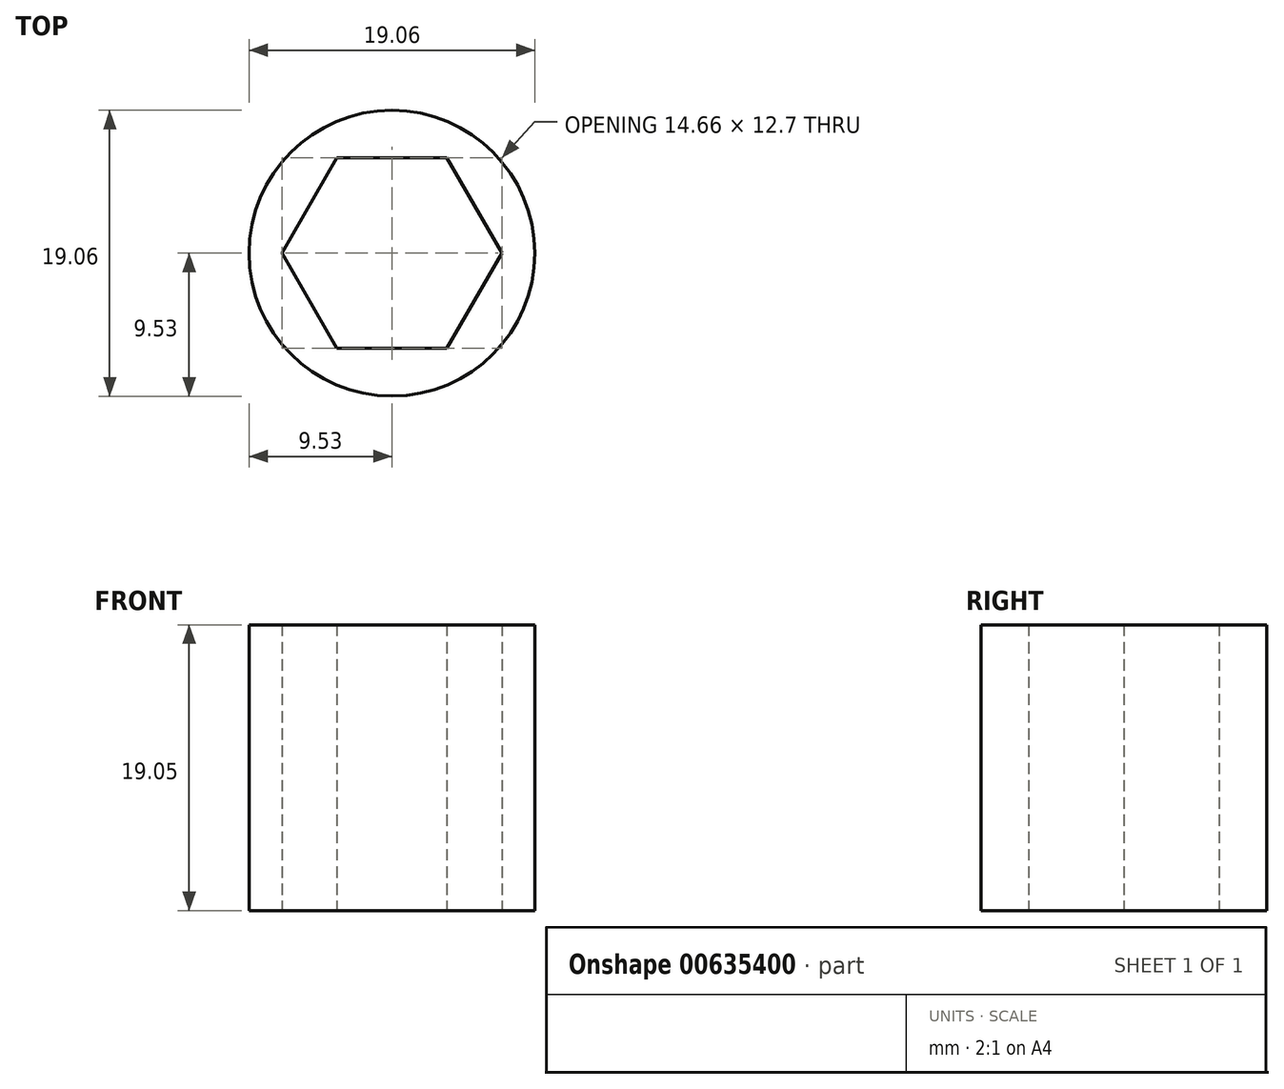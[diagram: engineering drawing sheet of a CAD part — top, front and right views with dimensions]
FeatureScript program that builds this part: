
annotation { "Feature Type Name" : "Feature", "Feature Type Description" : "" }
export const myFeature = defineFeature(function(context is Context, id is Id, definition is map)
    precondition{}
    {
        {
            var Q0;
            Q0=qCreatedBy(makeId("Top.planeOp"),FACE);
            var sketch = newSketch(context, id + "F0", { "sketchPlane" : qUnion([Q0])});
            skCircle(sketch, "E0.cCircle", {"center": v(0, 0) * mm, "radius": 6.35 * mm, "construction": true});
            skLineSegment(sketch, "E0.0", {"start": v(-3.67, 6.35) * mm, "end": v(3.67, 6.35) * mm});
            skLineSegment(sketch, "E0.1", {"start": v(3.67, 6.35) * mm, "end": v(7.33, 0) * mm});
            skLineSegment(sketch, "E0.2", {"start": v(7.33, 0) * mm, "end": v(3.67, -6.35) * mm});
            skLineSegment(sketch, "E0.3", {"start": v(3.67, -6.35) * mm, "end": v(-3.67, -6.35) * mm});
            skLineSegment(sketch, "E0.4", {"start": v(-3.67, -6.35) * mm, "end": v(-7.33, 0) * mm});
            skLineSegment(sketch, "E0.5", {"start": v(-7.33, 0) * mm, "end": v(-3.67, 6.35) * mm});
            skPoint(sketch, "E0.0.midPoint", {"position": v(0, 6.35) * mm});
            skCircle(sketch, "E1", {"center": v(0, 0) * mm, "radius": 9.53 * mm});
            skSolve(sketch);
        }
        {
            var Q0;
            Q0=qSketchRegion(id+"F0",true);
            extrude(context, id + "F1", {"entities" : qUnion([Q0]), "depth" : 19.05 * mm});
        }
    });
